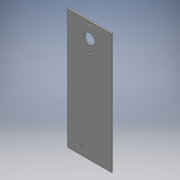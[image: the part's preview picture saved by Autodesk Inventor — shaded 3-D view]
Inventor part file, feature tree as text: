
AUTODESK INVENTOR PART (.ipt)
format: ipt  version: 2016 (Build 200138000, 138)  size: 119,296 bytes
history: native  units: mm
features: extrude x2, sketch x2, other x1
ambient origin geometry x8: Origin, YZ Plane, XZ Plane, XY Plane, X Axis, Y Axis, Z Axis, Center Point
bodies: Body1 (feature_tree)
feature tree (5):
  other  "ソリッド1"
  extrude  "押し出し1"  Depth=84.0mm
  extrude  "押し出し5"  Depth=230.0mm
  sketch  "スケッチ1"
  sketch  "スケッチ2"
